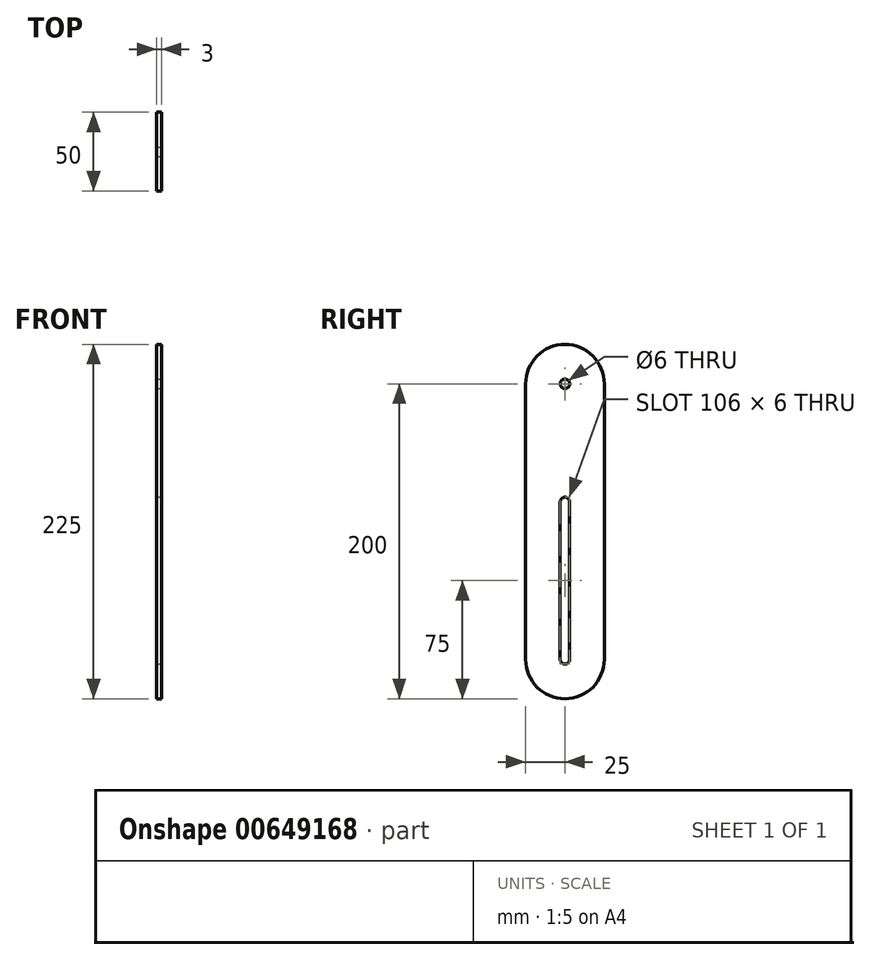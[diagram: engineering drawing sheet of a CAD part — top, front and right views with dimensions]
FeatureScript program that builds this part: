
annotation { "Feature Type Name" : "Feature", "Feature Type Description" : "" }
export const myFeature = defineFeature(function(context is Context, id is Id, definition is map)
    precondition{}
    {
        {
            var Q0;
            Q0=qCreatedBy(makeId("Right.planeOp"),FACE);
            var sketch = newSketch(context, id + "F0", { "sketchPlane" : qUnion([Q0])});
            skLineSegment(sketch, "E0.bottom", {"start": v(25, 200) * mm, "end": v(-25, 200) * mm});
            skLineSegment(sketch, "E0.top", {"start": v(25, -200) * mm, "end": v(-25, -200) * mm});
            skLineSegment(sketch, "E0.left", {"start": v(25, 200) * mm, "end": v(25, -200) * mm});
            skLineSegment(sketch, "E0.right", {"start": v(-25, 200) * mm, "end": v(-25, -200) * mm});
            skPoint(sketch, "E0.middle", {"position": v(0, 0) * mm});
            skSolve(sketch);
        }
        {
            var Q0;
            Q0 = qSketchRegion(id + "F0", true);
            extrude(context, id + "F1", {"entities" : qUnion([Q0]), "depth" : 3 * mm, "offsetDistance" : 25 * mm});
        }
        {
            var Q0;
            Q0=makeQuery(id+"F1.opExtrude","SWEPT_EDGE",EDGE,{"disambiguationData":[OSD([sQuery(id+"F0.wireOp",EDGE,"E0.bottom"),sQuery(id+"F0.wireOp",EDGE,"E0.right")])]});
            var Q1;
            Q1=makeQuery(id+"F1.opExtrude","SWEPT_EDGE",EDGE,{"disambiguationData":[OSD([sQuery(id+"F0.wireOp",EDGE,"E0.top"),sQuery(id+"F0.wireOp",EDGE,"E0.right")])]});
            var Q2;
            Q2=makeQuery(id+"F1.opExtrude","SWEPT_EDGE",EDGE,{"disambiguationData":[OSD([sQuery(id+"F0.wireOp",EDGE,"E0.bottom"),sQuery(id+"F0.wireOp",EDGE,"E0.left")])]});
            var Q3;
            Q3=makeQuery(id+"F1.opExtrude","SWEPT_EDGE",EDGE,{"disambiguationData":[OSD([sQuery(id+"F0.wireOp",EDGE,"E0.top"),sQuery(id+"F0.wireOp",EDGE,"E0.left")])]});
            fillet(context, id + "F2", {"entities" : qUnion([Q0, Q1, Q2, Q3]), "radius" : 25 * mm, "tangentPropagation" : true, "allowEdgeOverflow" : false});
        }
        {
            var Q0;
            Q0=makeQuery(id+"F1.opExtrude","CAP_FACE",FACE,{"disambiguationData":[OSD([sQuery(id+"F0.wireOp",EDGE,"E0.bottom"),sQuery(id+"F0.wireOp",EDGE,"E0.top"),sQuery(id+"F0.wireOp",EDGE,"E0.left"),sQuery(id+"F0.wireOp",EDGE,"E0.right")])],"isStart":false});
            var sketch = newSketch(context, id + "F3", { "sketchPlane" : qUnion([Q0])});
            skLineSegment(sketch, "E1", {"start": v(-25, 175) * mm, "end": v(25, 175) * mm, "construction": true});
            skCircle(sketch, "E2", {"center": v(0, 175) * mm, "radius": 3 * mm});
            skSolve(sketch);
        }
        {
            var Q0;
            Q0 = qSketchRegion(id + "F3", true);
            extrude(context, id + "F4", {"entities" : qUnion([Q0]), "operationType" : NewBodyOperationType.REMOVE, "oppositeDirection" : true, "depth" : 25 * mm, "offsetDistance" : 25 * mm});
        }
        {
            var Q0;
            Q0=makeQuery(id+"F1.opExtrude","CAP_FACE",FACE,{"disambiguationData":[OSD([sQuery(id+"F0.wireOp",EDGE,"E0.bottom"),sQuery(id+"F0.wireOp",EDGE,"E0.top"),sQuery(id+"F0.wireOp",EDGE,"E0.left"),sQuery(id+"F0.wireOp",EDGE,"E0.right")])],"isStart":false});
            var sketch = newSketch(context, id + "F5", { "sketchPlane" : qUnion([Q0])});
            skLineSegment(sketch, "E3", {"start": v(-25, 175) * mm, "end": v(0, 175) * mm, "construction": true});
            skLineSegment(sketch, "E4", {"start": v(0, 175) * mm, "end": v(0, 100) * mm, "construction": true});
            skCircle(sketch, "E5", {"center": v(0, 100) * mm, "radius": 3 * mm});
            skLineSegment(sketch, "E6", {"start": v(0, 100) * mm, "end": v(0, 0) * mm, "construction": true});
            skCircle(sketch, "E7", {"center": v(0, 0) * mm, "radius": 3 * mm});
            skLineSegment(sketch, "E8", {"start": v(0, 100) * mm, "end": v(3, 100) * mm, "construction": true});
            skLineSegment(sketch, "E9", {"start": v(3, 100) * mm, "end": v(3, 0) * mm});
            skLineSegment(sketch, "E10.MirrorCS", {"start": v(-3, 100) * mm, "end": v(-3, 0) * mm});
            skSolve(sketch);
        }
        {
            var Q0;
            Q0 = qSketchRegion(id + "F5", true);
            extrude(context, id + "F6", {"entities" : qUnion([Q0]), "operationType" : NewBodyOperationType.REMOVE, "oppositeDirection" : true, "depth" : 25 * mm, "offsetDistance" : 25 * mm});
        }
        {
            var Q0;
            Q0=makeQuery(id+"F1.opExtrude","CAP_FACE",FACE,{"disambiguationData":[OSD([sQuery(id+"F0.wireOp",EDGE,"E0.bottom"),sQuery(id+"F0.wireOp",EDGE,"E0.top"),sQuery(id+"F0.wireOp",EDGE,"E0.left"),sQuery(id+"F0.wireOp",EDGE,"E0.right")])],"isStart":false});
            var sketch = newSketch(context, id + "F7", { "sketchPlane" : qUnion([Q0])});
            skArc(sketch, "E11", {"start": v(-25, 0) * mm, "mid": v(0, -25) * mm, "end": v(25, 0) * mm});
            skLineSegment(sketch, "E12", {"start": v(-25, 0) * mm, "end": v(-25, -175) * mm});
            skLineSegment(sketch, "E13", {"start": v(25, 0) * mm, "end": v(25, -175) * mm});
            skArc(sketch, "E14", {"start": v(-25, -175) * mm, "mid": v(0, -200) * mm, "end": v(25, -175) * mm});
            skSolve(sketch);
        }
        {
            var Q0;
            Q0 = qSketchRegion(id + "F7", true);
            extrude(context, id + "F8", {"entities" : qUnion([Q0]), "operationType" : NewBodyOperationType.REMOVE, "oppositeDirection" : true, "depth" : 25 * mm, "offsetDistance" : 25 * mm});
        }
    });
